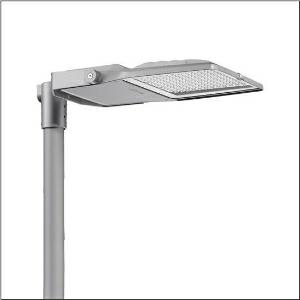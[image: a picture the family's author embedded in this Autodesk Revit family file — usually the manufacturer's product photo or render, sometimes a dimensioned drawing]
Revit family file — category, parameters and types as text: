
# Revit family: floodlight_fl_21_iq_midi___pl43_5xa7781f4a3a_cde7
name_source: partatom
category: Lighting Fixtures
units: mm (PartAtom-declared; Revit-internal decimal feet)

## family parameters
Cut with Voids When Loaded = No
Host = Face
Light Source = No
Part Type = Normal
Room Calculation Point = No
Round Connector Dimension = Use Diameter
Shared = No

## types (1)
- --- (1 x LED, 38290 lm, 270.2 W, 4000K)
    Apparent Load = 270 VA
    CIE Flux Codes = 27 78 99 100 100
    Color Rendering = 70
    Color Temperature = 4000K
    Default Elevation = 1800 mm
    Description = Floodlight FL 21 iQ midi, floodlight, primary light control with lens, of PMMA, primary optical cover: protective disc, of toughened safety glass, transparent, light distribution: PL43, light emission: direct distribution, installation type: surface-mounted, LED, High Power LED, rated luminous flux: 38.290lm, luminous efficacy: 142lm/W, light colour: 740, colour temperature: 4000K, control gear: iQ Comfort/DALI, control: optimised constant luminous flux control (CLO 2.0), Desk-Remote (wireless, voltage-free reading and setting of iQ features in the workshop via application-optimized NFC function/RFID function), Light-Fading, Smart-Wire, Night-Set, Lumen-Switch, Temp-Guard, Auto-Match, with terminal, 6-pole, mains connection: 220..240V, AC, 50/60Hz, start of lifetime: 270W, end of service life: 287W, reduction: 118W, luminaire housing, of diecast aluminium, powder-coated, Siteco® metallic grey (DB 702S), corrosivity category C5 mid according to DIN EN ISO 12944, suitable for swimming pools, chlorine-resistant, sealing non-destructively replaceable, please order mast flange separately, mast bracket, of steel, galvanised, powder-coated, Siteco® metallic grey (DB 702S), protection rating (complete): IP66, insulation class (complete): insulation class II (safety insulation), certification: CE, ENEC, VDE, protection symbol: D, impact resistance: IK08, permissible operating ambient temperature: -40..+40°C, permissible operating ambient temperature for outdoor applications: -40..+50°C, standard: DIN EN 12944, LABS conformity tested according to VDMA 24364:2018-05, packaging unit: 1 piece

Light Distribution: PL43
    Height = 76 mm
    Lamp = 1 x LED
    Lamp Light Flux = 38290 lm
    Lamp Power = 270.2 W
    Lamp count = 1
    Length = 657 mm
    Luminous efficacy = 142 lm/W
    Manufacturer = Siteco
    ModVariant = No
    Model = 5XA7781F4A3A
    Number of Poles = 1
    OnlyDefault = Yes
    Power Factor = 1
    Product Name = Floodlight FL 21 iQ midi | PL43
    Product group = floodlight | pylon annexe
    ProductGroupID = 6200
    Protection Class = Protection class II
    Protection Degree = IP 66
    RLX_Detail_Level = 1
    RLX_Emergency_Light_Flux = 0 lm
    RLX_Emergency_Type = 0
    RLX_Emergency_Type_DB = No
    RlxData = <blob elided: 153681 chars, md5=1008eaa6>
    Socket = socket
    Standby Power = 0 W
    System Light Flux = 38290 lm
    System Power = 270 W
    Type Comments = factory setting: luminous flux: 100 % | dim-lin: 254 | 620 mA
    Type Image = l_1007123.jpg
    URL = http://relux.com
    VarID = @adj_104812
    Voltage = 0 V
    Weight = 0.00 kg
    Width = 442 mm

## geometry (parser evidence)
native form markers: Blend x4, Sweep x11
no freeform markers — native parametric forms only
